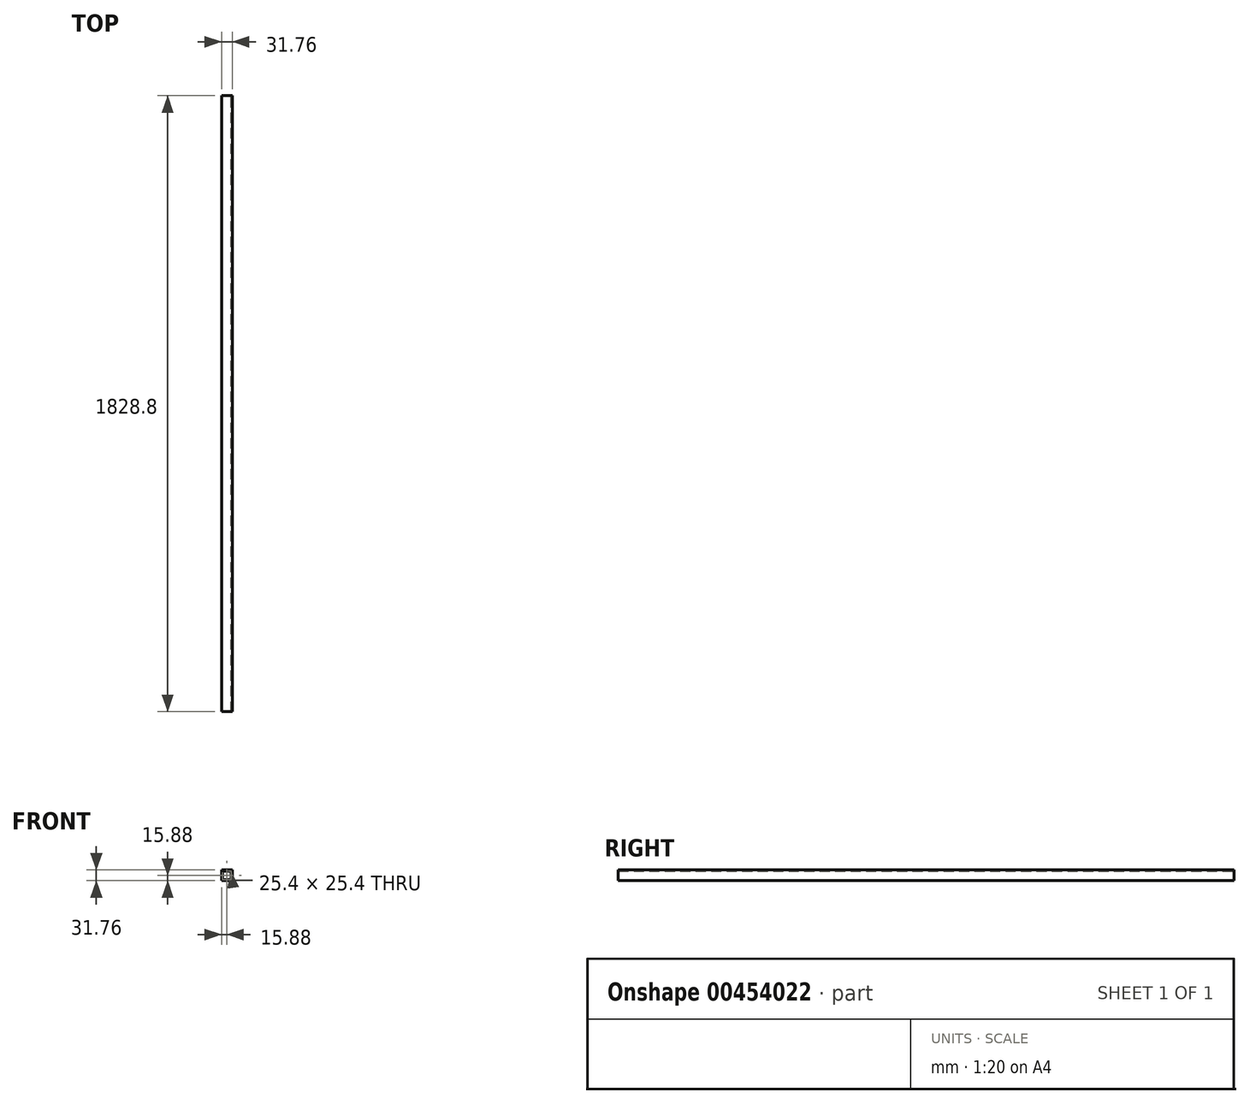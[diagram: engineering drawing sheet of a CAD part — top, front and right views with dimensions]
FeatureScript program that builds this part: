
annotation { "Feature Type Name" : "Feature", "Feature Type Description" : "" }
export const myFeature = defineFeature(function(context is Context, id is Id, definition is map)
    precondition{}
    {
        {
            var Q0;
            Q0=qCreatedBy(makeId("Front.planeOp"),FACE);
            var sketch = newSketch(context, id + "F0", { "sketchPlane" : qUnion([Q0])});
            skLineSegment(sketch, "E0.bottom", {"start": v(-15.87, 15.88) * mm, "end": v(15.88, 15.88) * mm});
            skLineSegment(sketch, "E0.top", {"start": v(-15.88, -15.88) * mm, "end": v(15.87, -15.88) * mm});
            skLineSegment(sketch, "E0.left", {"start": v(-15.87, 15.88) * mm, "end": v(-15.88, -15.88) * mm});
            skLineSegment(sketch, "E0.right", {"start": v(15.88, 15.88) * mm, "end": v(15.87, -15.88) * mm});
            skPoint(sketch, "E0.middle", {"position": v(0, 0) * mm});
            skLineSegment(sketch, "E1.bottom", {"start": v(-12.7, 12.7) * mm, "end": v(12.7, 12.7) * mm});
            skLineSegment(sketch, "E1.top", {"start": v(-12.7, -12.7) * mm, "end": v(12.7, -12.7) * mm});
            skLineSegment(sketch, "E1.left", {"start": v(-12.7, 12.7) * mm, "end": v(-12.7, -12.7) * mm});
            skLineSegment(sketch, "E1.right", {"start": v(12.7, 12.7) * mm, "end": v(12.7, -12.7) * mm});
            skSolve(sketch);
        }
        {
            var Q0;
            Q0=makeQuery(id+"F0.imprint","IMPRINT",FACE,{"disambiguationData":[TD([[makeQuery(id+"F0.imprint","IMPRINT",EDGE,{"derivedFrom":sQuery(id+"F0.wireOp",EDGE,"E0.bottom")}),-1.0]])]});
            extrude(context, id + "F1", {"entities" : qUnion([Q0]), "endBound" : BoundingType.SYMMETRIC, "depth" : 1828.8 * mm});
        }
    });
